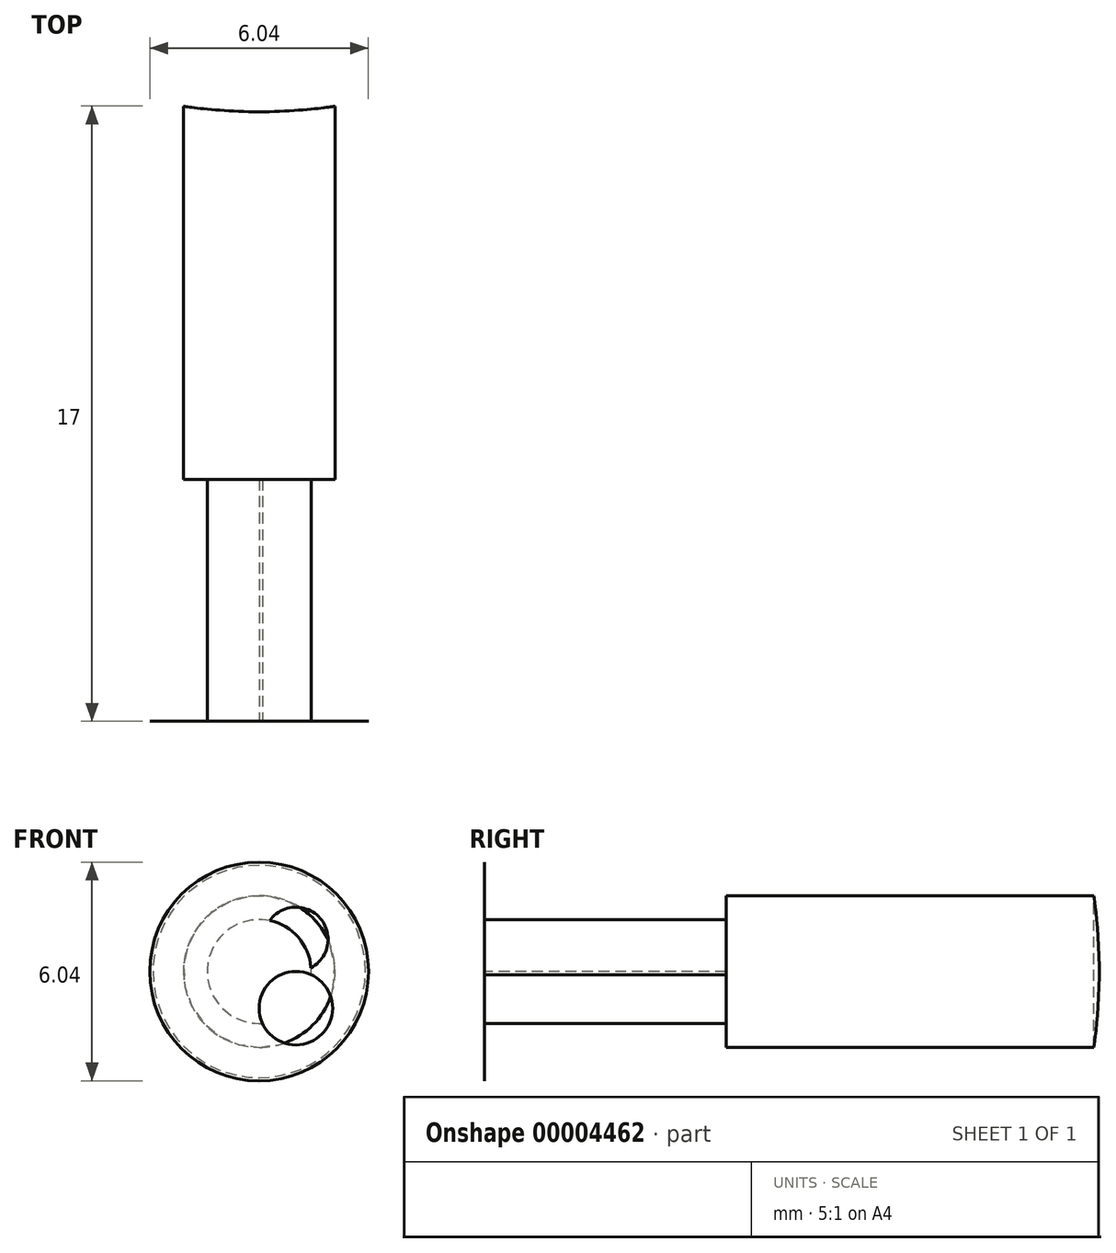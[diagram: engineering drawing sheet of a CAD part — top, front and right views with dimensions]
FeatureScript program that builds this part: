
annotation { "Feature Type Name" : "Feature", "Feature Type Description" : "" }
export const myFeature = defineFeature(function(context is Context, id is Id, definition is map)
    precondition{}
    {
        {
            var Q0;
            Q0=qCreatedBy(makeId("Front.planeOp"),FACE);
            var sketch = newSketch(context, id + "F0", { "sketchPlane" : qUnion([Q0])});
            skCircle(sketch, "E0", {"center": v(0, 0) * mm, "radius": 1.44 * mm});
            skCircle(sketch, "E1", {"center": v(0, 0) * mm, "radius": 3.02 * mm});
            skLineSegment(sketch, "E2", {"start": v(0, 0) * mm, "end": v(-2.14, 2.14) * mm, "construction": true});
            skLineSegment(sketch, "E3", {"start": v(0, 0) * mm, "end": v(2.14, 2.14) * mm, "construction": true});
            skLineSegment(sketch, "E4", {"start": v(0, 0) * mm, "end": v(2.14, -2.14) * mm, "construction": true});
            skLineSegment(sketch, "E5", {"start": v(0, 0) * mm, "end": v(-2.14, -2.14) * mm, "construction": true});
            skLineSegment(sketch, "E6", {"start": v(0, 0) * mm, "end": v(-3.02, 0) * mm, "construction": true});
            skArc(sketch, "E7", {"start": v(-1.01, 0) * mm, "mid": v(-0.18, 1.19) * mm, "end": v(-1.58, 1.58) * mm});
            skArc(sketch, "E8", {"start": v(-1.73, -1.73) * mm, "mid": v(-0.08, -1.4) * mm, "end": v(-1.01, 0) * mm});
            skCircle(sketch, "E9", {"center": v(1.01, 0.89) * mm, "radius": 0.89 * mm});
            skCircle(sketch, "E10", {"center": v(1.01, -1.01) * mm, "radius": 1.01 * mm});
            skSolve(sketch);
        }
        {
            var Q0;
            {var subQ0=sQuery(id+"F0.wireOp",EDGE,"E9");var subQ2=sQuery(id+"F0.wireOp",EDGE,"E0");var subQ4=makeQuery(id+"F0.imprint","INTERSECT",VERTEX,{"disambiguationData":[OD(0.0)],"derivedFrom":[subQ2,subQ0]});Q0=makeQuery(id+"F0.imprint","IMPRINT",FACE,{"disambiguationData":[TD([[makeQuery(id+"F0.imprint","IMPRINT",EDGE,{"disambiguationData":[TD([[subQ4,1.0]])],"derivedFrom":subQ2}),1.0]])]});}
            var Q1;
            {var subQ1=sQuery(id+"F0.wireOp",EDGE,"E9");var subQ3=sQuery(id+"F0.wireOp",EDGE,"E0");var subQ5=makeQuery(id+"F0.imprint","INTERSECT",VERTEX,{"disambiguationData":[OD(1.0)],"derivedFrom":[subQ3,subQ1]});Q1=makeQuery(id+"F0.imprint","IMPRINT",FACE,{"disambiguationData":[TD([[makeQuery(id+"F0.imprint","IMPRINT",EDGE,{"disambiguationData":[TD([[subQ5,1.0]])],"derivedFrom":subQ3}),1.0]])]});}
            var Q2;
            {var subQ5=sQuery(id+"F0.wireOp",EDGE,"E0");var subQ7=sQuery(id+"F0.wireOp",EDGE,"E7");var subQ9=makeQuery(id+"F0.imprint","INTERSECT",VERTEX,{"derivedFrom":[subQ5,subQ7]});Q2=makeQuery(id+"F0.imprint","IMPRINT",FACE,{"disambiguationData":[TD([[makeQuery(id+"F0.imprint","IMPRINT",EDGE,{"disambiguationData":[TD([[subQ9,1.0]])],"derivedFrom":subQ5}),1.0]])]});}
            var Q3;
            {var subQ2=sQuery(id+"F0.wireOp",EDGE,"E7");var subQ4=sQuery(id+"F0.wireOp",EDGE,"E0");var subQ6=makeQuery(id+"F0.imprint","INTERSECT",VERTEX,{"derivedFrom":[subQ4,subQ2]});Q3=makeQuery(id+"F0.imprint","IMPRINT",FACE,{"disambiguationData":[TD([[makeQuery(id+"F0.imprint","IMPRINT",EDGE,{"disambiguationData":[TD([[subQ6,-1.0]])],"derivedFrom":subQ4}),1.0]])]});}
            var Q4;
            {var subQ0=sQuery(id+"F0.wireOp",EDGE,"E10");var subQ2=sQuery(id+"F0.wireOp",EDGE,"E0");var subQ3=makeQuery(id+"F0.imprint","INTERSECT",VERTEX,{"disambiguationData":[OD(0.0)],"derivedFrom":[subQ2,subQ0]});Q4=makeQuery(id+"F0.imprint","IMPRINT",FACE,{"disambiguationData":[TD([[makeQuery(id+"F0.imprint","IMPRINT",EDGE,{"disambiguationData":[TD([[subQ3,-1.0]])],"derivedFrom":subQ2}),1.0]])]});}
            var Q5;
            {var subQ1=sQuery(id+"F0.wireOp",EDGE,"E8");var subQ3=sQuery(id+"F0.wireOp",EDGE,"E0");var subQ5=makeQuery(id+"F0.imprint","INTERSECT",VERTEX,{"derivedFrom":[subQ3,subQ1]});Q5=makeQuery(id+"F0.imprint","IMPRINT",FACE,{"disambiguationData":[TD([[makeQuery(id+"F0.imprint","IMPRINT",EDGE,{"disambiguationData":[TD([[subQ5,-1.0]])],"derivedFrom":subQ3}),1.0]])]});}
            extrude(context, id + "F1", {"entities" : qUnion([Q0, Q1, Q2, Q3, Q4, Q5]), "oppositeDirection" : true, "depth" : 6.68 * mm});
        }
        {
            var Q0;
            Q0=makeQuery(id+"F0.imprint","IMPRINT",FACE,{"disambiguationData":[TD([[makeQuery(id+"F0.imprint","IMPRINT",EDGE,{"derivedFrom":sQuery(id+"F0.wireOp",EDGE,"E1")}),1.0]])]});
            var Q1;
            {var subQ2=sQuery(id+"F0.wireOp",EDGE,"E7");var subQ4=sQuery(id+"F0.wireOp",EDGE,"E0");var subQ6=makeQuery(id+"F0.imprint","INTERSECT",VERTEX,{"derivedFrom":[subQ4,subQ2]});Q1=makeQuery(id+"F0.imprint","IMPRINT",FACE,{"disambiguationData":[TD([[makeQuery(id+"F0.imprint","IMPRINT",EDGE,{"disambiguationData":[TD([[subQ6,-1.0]])],"derivedFrom":subQ4}),1.0]])]});}
            var Q2;
            {var subQ5=sQuery(id+"F0.wireOp",EDGE,"E0");var subQ7=sQuery(id+"F0.wireOp",EDGE,"E7");var subQ9=makeQuery(id+"F0.imprint","INTERSECT",VERTEX,{"derivedFrom":[subQ5,subQ7]});Q2=makeQuery(id+"F0.imprint","IMPRINT",FACE,{"disambiguationData":[TD([[makeQuery(id+"F0.imprint","IMPRINT",EDGE,{"disambiguationData":[TD([[subQ9,1.0]])],"derivedFrom":subQ5}),1.0]])]});}
            var Q3;
            {var subQ0=sQuery(id+"F0.wireOp",EDGE,"E9");var subQ2=sQuery(id+"F0.wireOp",EDGE,"E0");var subQ4=makeQuery(id+"F0.imprint","INTERSECT",VERTEX,{"disambiguationData":[OD(0.0)],"derivedFrom":[subQ2,subQ0]});Q3=makeQuery(id+"F0.imprint","IMPRINT",FACE,{"disambiguationData":[TD([[makeQuery(id+"F0.imprint","IMPRINT",EDGE,{"disambiguationData":[TD([[subQ4,1.0]])],"derivedFrom":subQ2}),1.0]])]});}
            var Q4;
            {var subQ0=sQuery(id+"F0.wireOp",EDGE,"E10");var subQ2=sQuery(id+"F0.wireOp",EDGE,"E0");var subQ3=makeQuery(id+"F0.imprint","INTERSECT",VERTEX,{"disambiguationData":[OD(0.0)],"derivedFrom":[subQ2,subQ0]});Q4=makeQuery(id+"F0.imprint","IMPRINT",FACE,{"disambiguationData":[TD([[makeQuery(id+"F0.imprint","IMPRINT",EDGE,{"disambiguationData":[TD([[subQ3,-1.0]])],"derivedFrom":subQ2}),1.0]])]});}
            var Q5;
            {var subQ0=sQuery(id+"F0.wireOp",EDGE,"E10");var subQ1=sQuery(id+"F0.wireOp",EDGE,"E0");var subQ3=makeQuery(id+"F0.imprint","INTERSECT",VERTEX,{"disambiguationData":[OD(0.0)],"derivedFrom":[subQ1,subQ0]});Q5=makeQuery(id+"F0.imprint","IMPRINT",FACE,{"disambiguationData":[TD([[makeQuery(id+"F0.imprint","IMPRINT",EDGE,{"disambiguationData":[TD([[subQ3,-1.0]])],"derivedFrom":subQ1}),-1.0]])]});}
            var Q6;
            {var subQ0=sQuery(id+"F0.wireOp",EDGE,"E9");var subQ1=sQuery(id+"F0.wireOp",EDGE,"E0");var subQ3=makeQuery(id+"F0.imprint","INTERSECT",VERTEX,{"disambiguationData":[OD(0.0)],"derivedFrom":[subQ1,subQ0]});Q6=makeQuery(id+"F0.imprint","IMPRINT",FACE,{"disambiguationData":[TD([[makeQuery(id+"F0.imprint","IMPRINT",EDGE,{"disambiguationData":[TD([[subQ3,1.0]])],"derivedFrom":subQ1}),-1.0]])]});}
            var Q7;
            {var subQ1=sQuery(id+"F0.wireOp",EDGE,"E8");var subQ3=sQuery(id+"F0.wireOp",EDGE,"E0");var subQ5=makeQuery(id+"F0.imprint","INTERSECT",VERTEX,{"derivedFrom":[subQ3,subQ1]});Q7=makeQuery(id+"F0.imprint","IMPRINT",FACE,{"disambiguationData":[TD([[makeQuery(id+"F0.imprint","IMPRINT",EDGE,{"disambiguationData":[TD([[subQ5,-1.0]])],"derivedFrom":subQ3}),1.0]])]});}
            var Q8;
            {var subQ1=sQuery(id+"F0.wireOp",EDGE,"E9");var subQ3=sQuery(id+"F0.wireOp",EDGE,"E0");var subQ5=makeQuery(id+"F0.imprint","INTERSECT",VERTEX,{"disambiguationData":[OD(1.0)],"derivedFrom":[subQ3,subQ1]});Q8=makeQuery(id+"F0.imprint","IMPRINT",FACE,{"disambiguationData":[TD([[makeQuery(id+"F0.imprint","IMPRINT",EDGE,{"disambiguationData":[TD([[subQ5,1.0]])],"derivedFrom":subQ3}),1.0]])]});}
            var Q9;
            Q9=sQuery(id+"F0.wireOp",EDGE,"E1");
            extrude(context, id + "F2", {"entities" : qUnion([Q0, Q1, Q2, Q3, Q4, Q5, Q6, Q7, Q8]), "operationType" : NewBodyOperationType.ADD, "surfaceEntities" : qUnion([Q9]), "oppositeDirection" : true, "depth" : 1 / 406.4 * mm});
        }
        {
            var Q0;
            Q0=makeQuery(id+"F1.opExtrude","CAP_FACE",FACE,{"disambiguationData":[OSD([sQuery(id+"F0.wireOp",EDGE,"E0")])],"isStart":false});
            var sketch = newSketch(context, id + "F3", { "sketchPlane" : qUnion([Q0])});
            skCircle(sketch, "E11", {"center": v(0, 0) * mm, "radius": 2.1 * mm});
            skSolve(sketch);
        }
        {
            var Q0;
            Q0=makeQuery(id+"F3.imprint","IMPRINT",FACE,{"disambiguationData":[TD([[makeQuery(id+"F3.imprint","IMPRINT",EDGE,{"derivedFrom":sQuery(id+"F3.wireOp",EDGE,"E11")}),1.0]])]});
            var Q1;
            Q1=makeQuery(id+"F3.imprint","IMPRINT",FACE,{"disambiguationData":[TD([[makeQuery(id+"F3.imprint","IMPRINT",EDGE,{"derivedFrom":makeQuery(id+"F1.opExtrude","CAP_EDGE",EDGE,{"disambiguationData":[OSD([sQuery(id+"F0.wireOp",EDGE,"E0")])],"isStart":false})}),-1.0]])]});
            var Q2;
            Q2=sQuery(id+"F3.wireOp",EDGE,"E11");
            extrude(context, id + "F4", {"entities" : qUnion([Q0, Q1]), "operationType" : NewBodyOperationType.ADD, "surfaceEntities" : qUnion([Q2]), "depth" : 12.7 * mm});
        }
        {
            var Q0;
            Q0=qCreatedBy(makeId("Right.planeOp"),FACE);
            var sketch = newSketch(context, id + "F5", { "sketchPlane" : qUnion([Q0])});
            skCircle(sketch, "E12", {"center": v(1.59, 3.02) * mm, "radius": 1.59 * mm});
            skLineSegment(sketch, "E13", {"start": v(0, 0) * mm, "end": v(1.59, 0) * mm, "construction": true});
            skSolve(sketch);
        }
        {
            var Q0;
            Q0=makeQuery(id+"F5.imprint","IMPRINT",FACE,{"disambiguationData":[TD([[makeQuery(id+"F5.imprint","IMPRINT",EDGE,{"derivedFrom":sQuery(id+"F5.wireOp",EDGE,"E12")}),1.0]])]});
            var Q1;
            Q1=sQuery(id+"F5.wireOp",EDGE,"E12");
            var Q2;
            Q2=sQuery(id+"F5.wireOp",EDGE,"E13");
            revolve(context, id + "F6", {"operationType" : NewBodyOperationType.REMOVE, "entities" : qUnion([Q0]), "surfaceEntities" : qUnion([Q1]), "axis" : qUnion([Q2]), "revolveType" : RevolveType.FULL, "oppositeDirection" : true});
        }
        {
            var Q0;
            Q0=qCreatedBy(makeId("Top.planeOp"),FACE);
            var sketch = newSketch(context, id + "F7", { "sketchPlane" : qUnion([Q0])});
            skCircle(sketch, "E14", {"center": v(0, 31.13) * mm, "radius": 14.29 * mm});
            skSolve(sketch);
        }
        {
            var Q0;
            Q0=makeQuery(id+"F7.imprint","IMPRINT",FACE,{"disambiguationData":[TD([[makeQuery(id+"F7.imprint","IMPRINT",EDGE,{"derivedFrom":sQuery(id+"F7.wireOp",EDGE,"E14")}),1.0]])]});
            var Q1;
            Q1=sQuery(id+"F7.wireOp",EDGE,"E14");
            extrude(context, id + "F8", {"entities" : qUnion([Q0]), "operationType" : NewBodyOperationType.REMOVE, "surfaceEntities" : qUnion([Q1]), "oppositeDirection" : true, "depth" : 4.2 * mm, "symmetric" : true});
        }
    });
